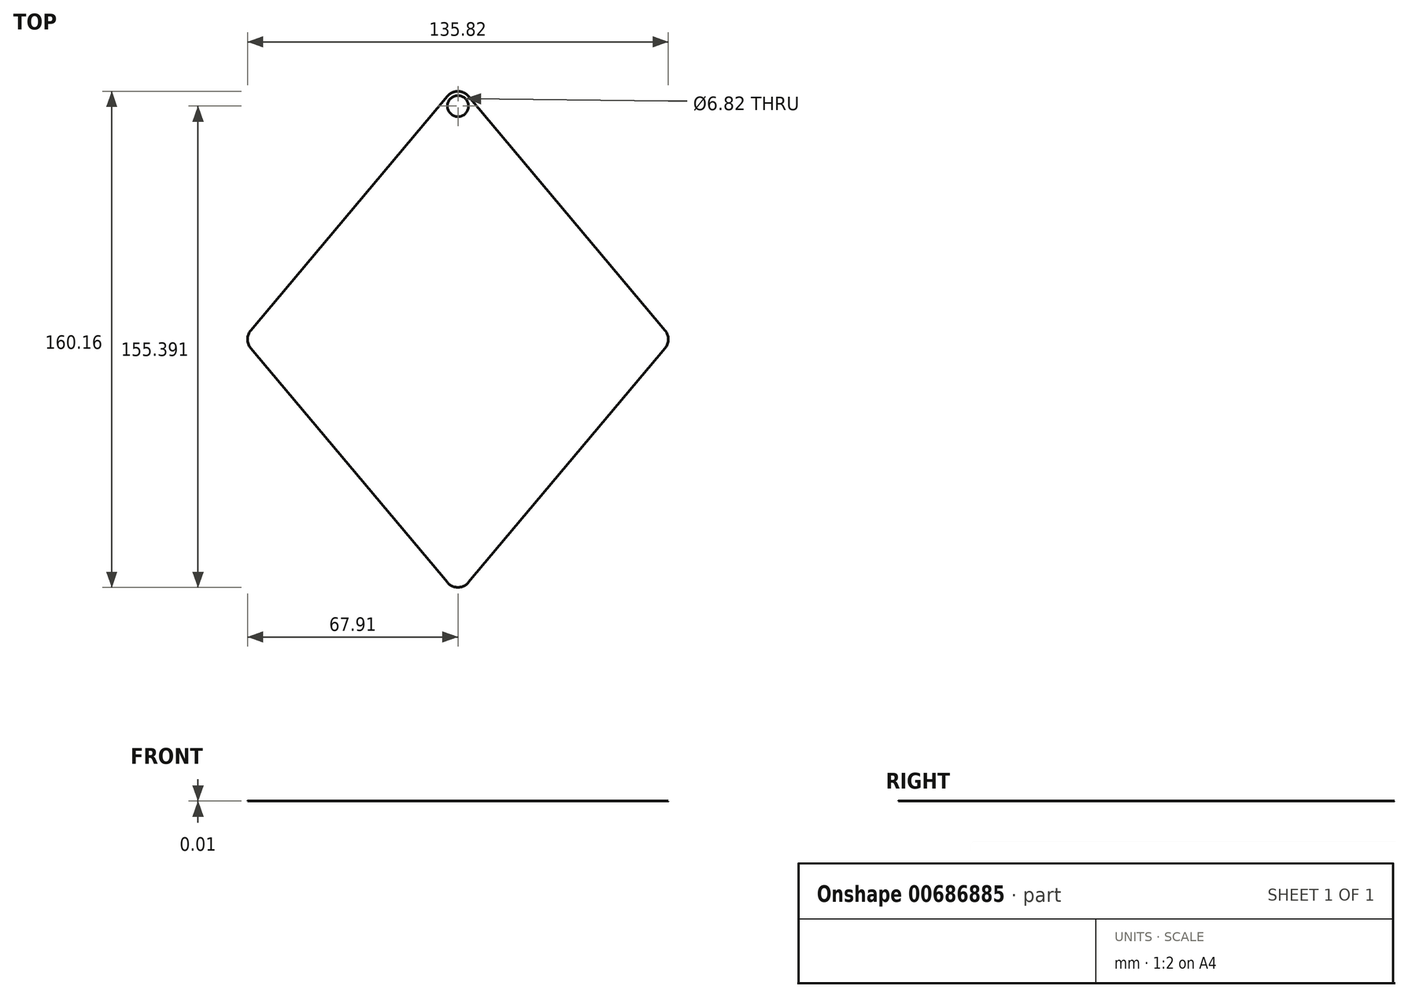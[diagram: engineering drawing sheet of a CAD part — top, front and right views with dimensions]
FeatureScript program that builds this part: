
annotation { "Feature Type Name" : "Feature", "Feature Type Description" : "" }
export const myFeature = defineFeature(function(context is Context, id is Id, definition is map)
    precondition{}
    {
        {
            var Q0;
            Q0=qCreatedBy(makeId("Top.planeOp"),FACE);
            var sketch = newSketch(context, id + "F0", { "sketchPlane" : qUnion([Q0])});
            skLineSegment(sketch, "E0", {"start": v(-3.4, 78.5) * mm, "end": v(-66.87, 2.86) * mm});
            skLineSegment(sketch, "E1", {"start": v(-66.87, -2.86) * mm, "end": v(-3.4, -78.5) * mm});
            skLineSegment(sketch, "E2", {"start": v(3.4, -78.5) * mm, "end": v(66.87, -2.86) * mm});
            skLineSegment(sketch, "E3", {"start": v(66.87, 2.86) * mm, "end": v(3.4, 78.5) * mm});
            skCircle(sketch, "E4", {"center": v(0, 75.31) * mm, "radius": 3.4 * mm});
            skPoint(sketch, "E5.visualSharp", {"position": v(0, 82.55) * mm});
            skArc(sketch, "E5.filletArc", {"start": v(3.4, 78.5) * mm, "mid": v(0, 80.08) * mm, "end": v(-3.4, 78.5) * mm});
            skPoint(sketch, "E6.visualSharp", {"position": v(69.27, 0) * mm});
            skArc(sketch, "E6.filletArc", {"start": v(66.87, -2.86) * mm, "mid": v(67.91, 0) * mm, "end": v(66.87, 2.86) * mm});
            skPoint(sketch, "E7.visualSharp", {"position": v(0, -82.55) * mm});
            skArc(sketch, "E7.filletArc", {"start": v(-3.4, -78.5) * mm, "mid": v(0, -80.08) * mm, "end": v(3.4, -78.5) * mm});
            skPoint(sketch, "E8.visualSharp", {"position": v(-69.27, 0) * mm});
            skArc(sketch, "E8.filletArc", {"start": v(-66.87, 2.86) * mm, "mid": v(-67.91, 0) * mm, "end": v(-66.87, -2.86) * mm});
            skSolve(sketch);
        }
        {
            var Q0;
            Q0=makeQuery(id+"F0.imprint","IMPRINT",FACE,{"disambiguationData":[TD([[makeQuery(id+"F0.imprint","IMPRINT",EDGE,{"derivedFrom":sQuery(id+"F0.wireOp",EDGE,"E0")}),1.0]])]});
            extrude(context, id + "F1", {"entities" : qUnion([Q0]), "depth" : 1 / 101.6 * mm, "offsetDistance" : 25.4 * mm});
        }
    });
